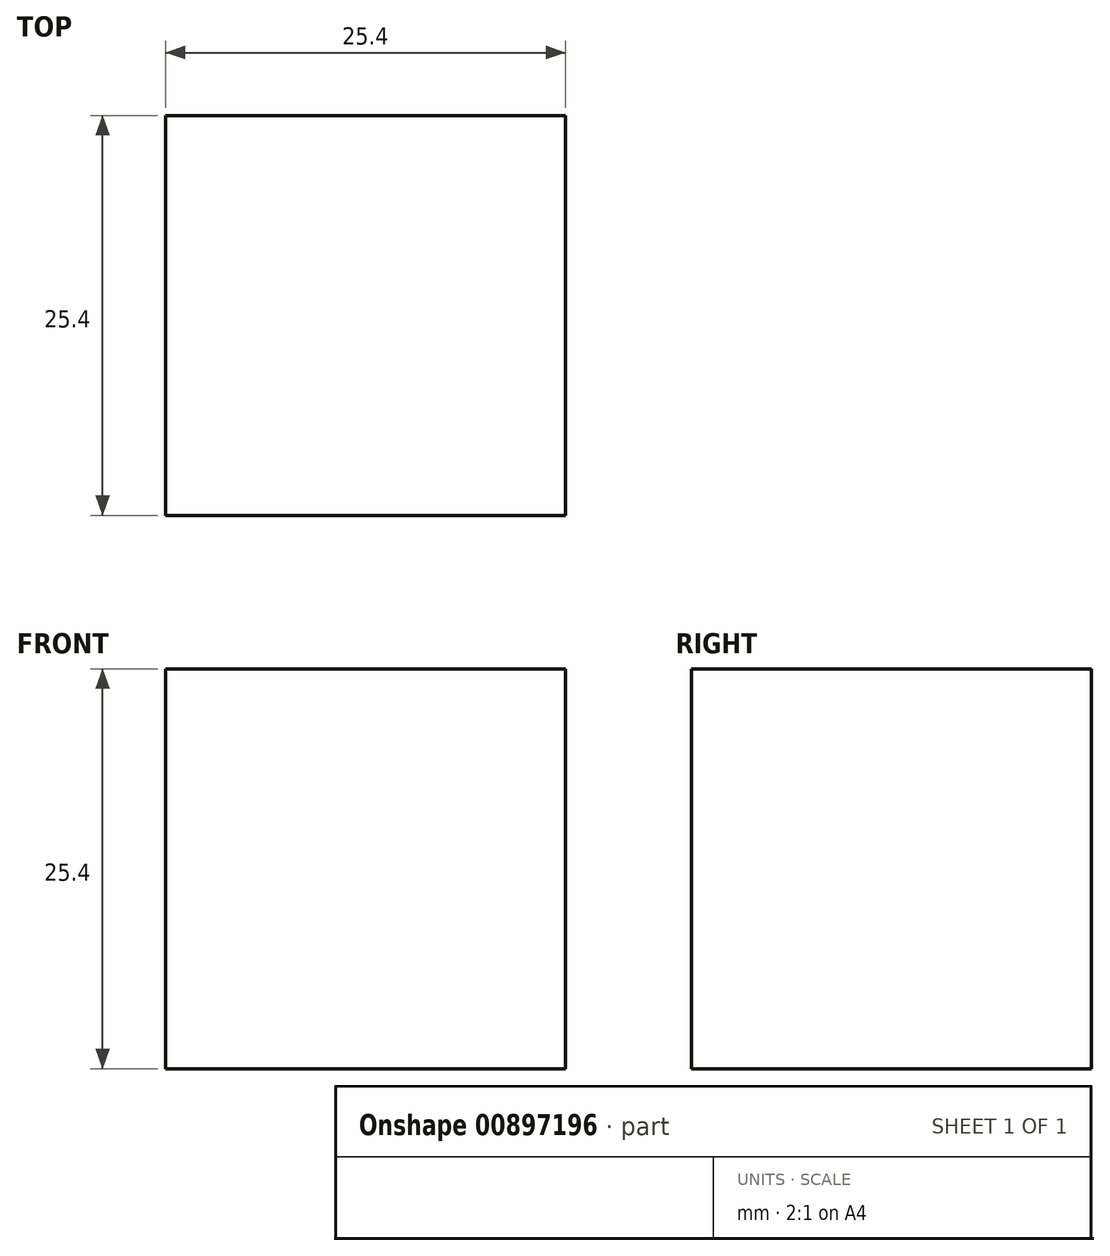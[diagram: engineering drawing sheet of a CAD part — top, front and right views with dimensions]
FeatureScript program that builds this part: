
annotation { "Feature Type Name" : "Feature", "Feature Type Description" : "" }
export const myFeature = defineFeature(function(context is Context, id is Id, definition is map)
    precondition{}
    {
        {
            var Q0;
            Q0=qCreatedBy(makeId("Top.planeOp"),FACE);
            var sketch = newSketch(context, id + "F0", { "sketchPlane" : qUnion([Q0])});
            skLineSegment(sketch, "E0", {"start": v(0, 0) * mm, "end": v(25.4, 0) * mm});
            skLineSegment(sketch, "E1", {"start": v(25.4, 0) * mm, "end": v(25.4, 25.4) * mm});
            skLineSegment(sketch, "E2", {"start": v(25.4, 25.4) * mm, "end": v(0, 25.4) * mm});
            skLineSegment(sketch, "E3", {"start": v(0, 25.4) * mm, "end": v(0, 0) * mm});
            skSolve(sketch);
        }
        {
            var Q0;
            Q0=makeQuery(id+"F0.imprint","IMPRINT",FACE,{"disambiguationData":[TD([[makeQuery(id+"F0.imprint","IMPRINT",EDGE,{"derivedFrom":sQuery(id+"F0.wireOp",EDGE,"E0")}),1.0]])]});
            extrude(context, id + "F1", {"entities" : qUnion([Q0]), "depth" : 25.4 * mm, "offsetDistance" : 25.4 * mm});
        }
    });
